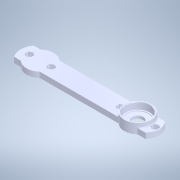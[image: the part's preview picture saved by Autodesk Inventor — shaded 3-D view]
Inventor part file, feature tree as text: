
AUTODESK INVENTOR PART (.ipt)
format: ipt  version: 2021 (Build 250183000, 183)  size: 351,232 bytes
history: native  units: in
note: dims shown in document units (in); Inventor stores cm internally (conversion verified against a paired STEP export)
features: sketch x14, extrude x11, fillet x2, projected_geometry x2, delete_face x1, chamfer x1, hole x1, other x1
ambient origin geometry x8: Origin, YZ Plane, XZ Plane, XY Plane, X Axis, Y Axis, Z Axis, Center Point
bodies: Solid1 (feature_tree)
feature tree (33):
  extrude  "Extrusion1"  Depth=0.3937in TaperAngle=0.0deg
  extrude  "Extrusion2"  TaperAngle=0.0deg  [1 undecoded]
  sketch  "Sketch5"  dims[d9=0.3937in d10=0.0in d11=0.878in d12=0.3937in d13=0.0in]
  delete_face  "Delete Face1"
  extrude  "Extrusion4"  Depth=0.3937in
  extrude  "Extrusion5"  Depth=0.3937in
  chamfer  "Chamfer1"  Distance=0.3937in
  sketch  "Sketch8"  dims[d32=0.3937in d33=0.0in d34=0.0787in d35=0.0787in d36=0.0in]
  extrude  "Extrusion7"  Depth=0.7087in
  extrude  "Extrusion9"  Depth=0.3937in
  extrude  "Extrusion8"  Depth=0.3937in
  fillet  "Fillet2"  Radius=0.0787in
  hole  "Hole1"  [1 undecoded]
  extrude  "Extrusion10"  Depth=0.2362in
  extrude  "Extrusion11"  Depth=1.1811in
  extrude  "Extrusion12"  Depth=0.3937in
  fillet  "Fillet3"  Radius=0.3937in
  extrude  "Extrusion3"  Depth=0.0118in
  sketch  "Sketch1"  dims[d0=0.7874in d1=0.3937in d2=0.0in]
  sketch  "Sketch2"  dims[d3=0.3937in d4=0.0in d5=0.0in]
  sketch  "Sketch4"  dims[d6=0.3937in d7=0.0in d8=0.9843in]
  sketch  "Sketch6"  dims[d14=0.0197in d15=0.0787in d16=45.0deg d28=0.7087in]
  sketch  "Sketch7"  dims[d29=0.3937in d30=0.0in d31=3.5433in]
  sketch  "Sketch11"  dims[d37=0.7874in d39=0.4921in]
  sketch  "Sketch12"  dims[d40=0.1378in d41=0.2362in d42=0.1575in d43=0.0787in d44=90.0deg d45=0.315in d46=0.8108in d47=0.2264in]
  sketch  "Sketch13"  dims[d48=0.0787in d49=0.0in d50=1.1811in]
  sketch  "Sketch14"  dims[d52=0.1181in d53=0.1378in d54=0.3937in d55=0.0in]
  projected_geometry  "Projected Loop3"
  projected_geometry  "Projected Loop4"
  sketch  "Sketch15"  dims[d56=0.0472in d57=0.0118in]
  sketch  "Sketch16"  dims[d60=0.0591in d61=0.0in]
  sketch  "Sketch17"  dims[d62=0.0394in]
  other  "Cut-Extrude3"
note: 2 required parameter values undecoded (feature->parameter linkage not recoverable at this tier; creation-order binding heuristic only, values carry confidence <= 0.55)
